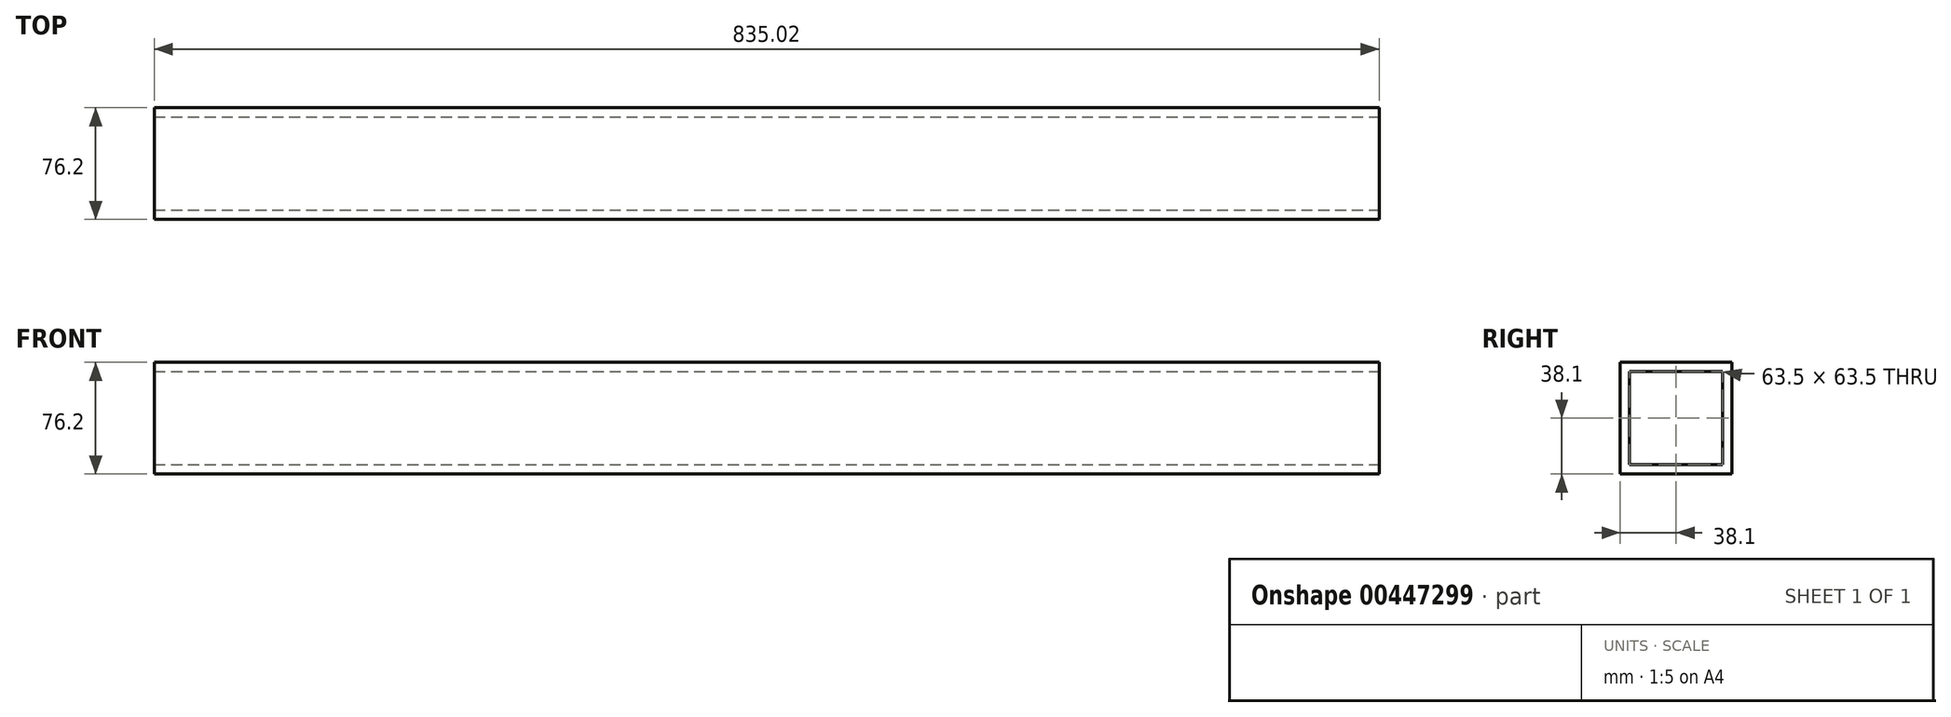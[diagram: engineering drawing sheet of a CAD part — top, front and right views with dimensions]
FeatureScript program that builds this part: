
annotation { "Feature Type Name" : "Feature", "Feature Type Description" : "" }
export const myFeature = defineFeature(function(context is Context, id is Id, definition is map)
    precondition{}
    {
        {
            var Q0;
            Q0=qCreatedBy(makeId("Front.planeOp"),FACE);
            var sketch = newSketch(context, id + "F0", { "sketchPlane" : qUnion([Q0])});
            skLineSegment(sketch, "E0.bottom", {"start": v(-417.51, -38.1) * mm, "end": v(417.51, -38.1) * mm});
            skLineSegment(sketch, "E0.top", {"start": v(-417.51, 38.1) * mm, "end": v(417.51, 38.1) * mm});
            skLineSegment(sketch, "E0.left", {"start": v(-417.51, -38.1) * mm, "end": v(-417.51, 38.1) * mm});
            skLineSegment(sketch, "E0.right", {"start": v(417.51, -38.1) * mm, "end": v(417.51, 38.1) * mm});
            skPoint(sketch, "E0.middle", {"position": v(0, 0) * mm});
            skSolve(sketch);
        }
        {
            var Q0;
            Q0 = qSketchRegion(id + "F0", true);
            extrude(context, id + "F1", {"entities" : qUnion([Q0]), "depth" : 76.2 * mm});
        }
        {
            var Q0;
            Q0=makeQuery(id+"F1.opExtrude","SWEPT_FACE",FACE,{"disambiguationData":[OSD([sQuery(id+"F0.wireOp",EDGE,"E0.right")])]});
            shell(context, id + "F2", {"entities" : qUnion([Q0]), "thickness" : 6.35 * mm});
        }
        {
            var Q0;
            Q0=makeQuery(id+"F1.opExtrude","SWEPT_FACE",FACE,{"disambiguationData":[OSD([sQuery(id+"F0.wireOp",EDGE,"E0.left")])]});
            var Q1;
            Q1=makeQuery(id+"F2.opShell","OFFSET_FACE",FACE,{"disambiguationData":[OSD([sQuery(id+"F0.wireOp",EDGE,"E0.left")])]});
            var Q2;
            {var subQ0=sQuery(id+"F0.wireOp",EDGE,"E0.right");var subQ1=sQuery(id+"F0.wireOp",EDGE,"E0.left");var subQ2=sQuery(id+"F0.wireOp",EDGE,"E0.top");var subQ3=sQuery(id+"F0.wireOp",EDGE,"E0.bottom");Q2=makeQuery(id+"F2.opShell","OFFSET_FACE",FACE,{"disambiguationData":[OSD([subQ3,subQ2,subQ1,subQ0]),TDD([makeQuery(id+"F1.opExtrude","CAP_FACE",FACE,{"disambiguationData":[OSD([subQ3,subQ2,subQ1,subQ0])],"isStart":true})])]});}
            shell(context, id + "F3", {"entities" : qUnion([Q0, Q1, Q2]), "thickness" : 6.35 * mm});
        }
    });
